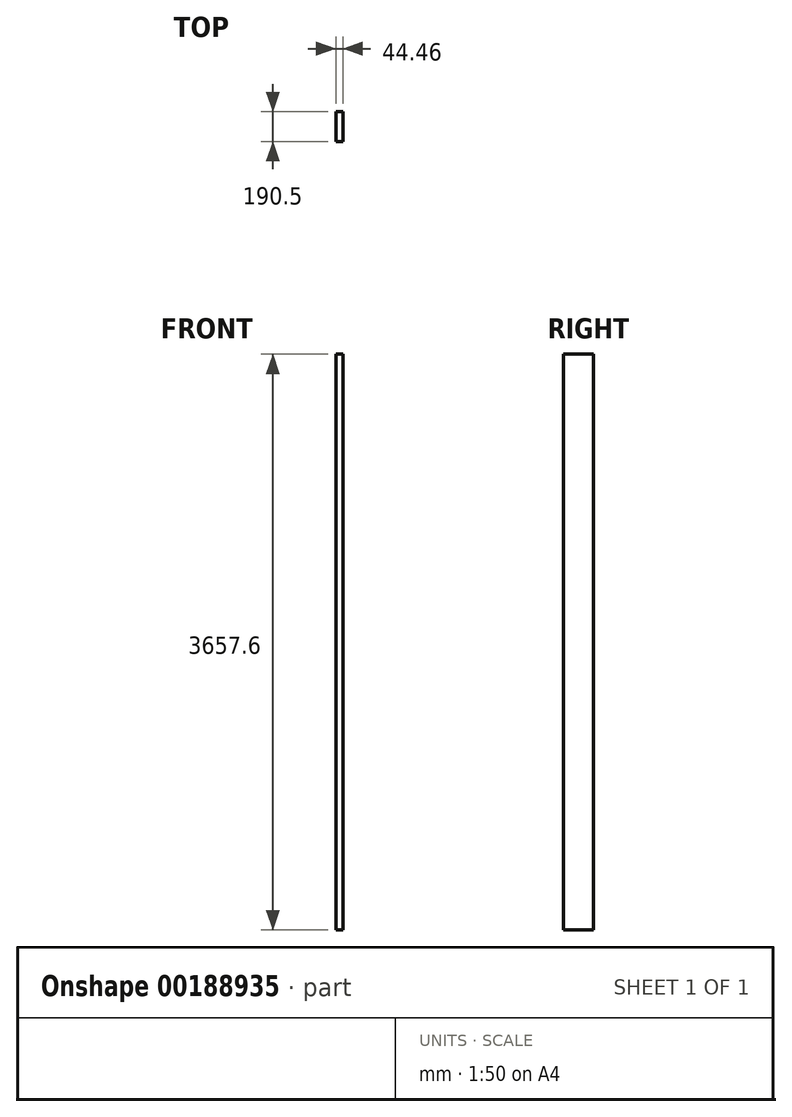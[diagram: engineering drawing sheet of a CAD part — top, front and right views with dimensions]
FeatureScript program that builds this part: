
annotation { "Feature Type Name" : "Feature", "Feature Type Description" : "" }
export const myFeature = defineFeature(function(context is Context, id is Id, definition is map)
    precondition{}
    {
        {
            var Q0;
            Q0=qCreatedBy(makeId("Top.planeOp"),FACE);
            var sketch = newSketch(context, id + "F1", { "sketchPlane" : qUnion([Q0])});
            skLineSegment(sketch, "E0.bottom", {"start": v(22.23, -95.25) * mm, "end": v(-22.22, -95.25) * mm});
            skLineSegment(sketch, "E0.top", {"start": v(22.22, 95.25) * mm, "end": v(-22.23, 95.25) * mm});
            skLineSegment(sketch, "E0.left", {"start": v(22.23, -95.25) * mm, "end": v(22.22, 95.25) * mm});
            skLineSegment(sketch, "E0.right", {"start": v(-22.22, -95.25) * mm, "end": v(-22.23, 95.25) * mm});
            skPoint(sketch, "E0.middle", {"position": v(0, 0) * mm});
            skSolve(sketch);
        }
        {
            var Q0;
            Q0=makeQuery(id+"F1.imprint","IMPRINT",FACE,{"disambiguationData":[TD([[makeQuery(id+"F1.imprint","IMPRINT",EDGE,{"derivedFrom":sQuery(id+"F1.wireOp",EDGE,"E0.bottom")}),-1.0]])]});
            extrude(context, id + "F0", {"entities" : qUnion([Q0]), "endBound" : BoundingType.SYMMETRIC, "depth" : 3657.6 * mm});
        }
    });
